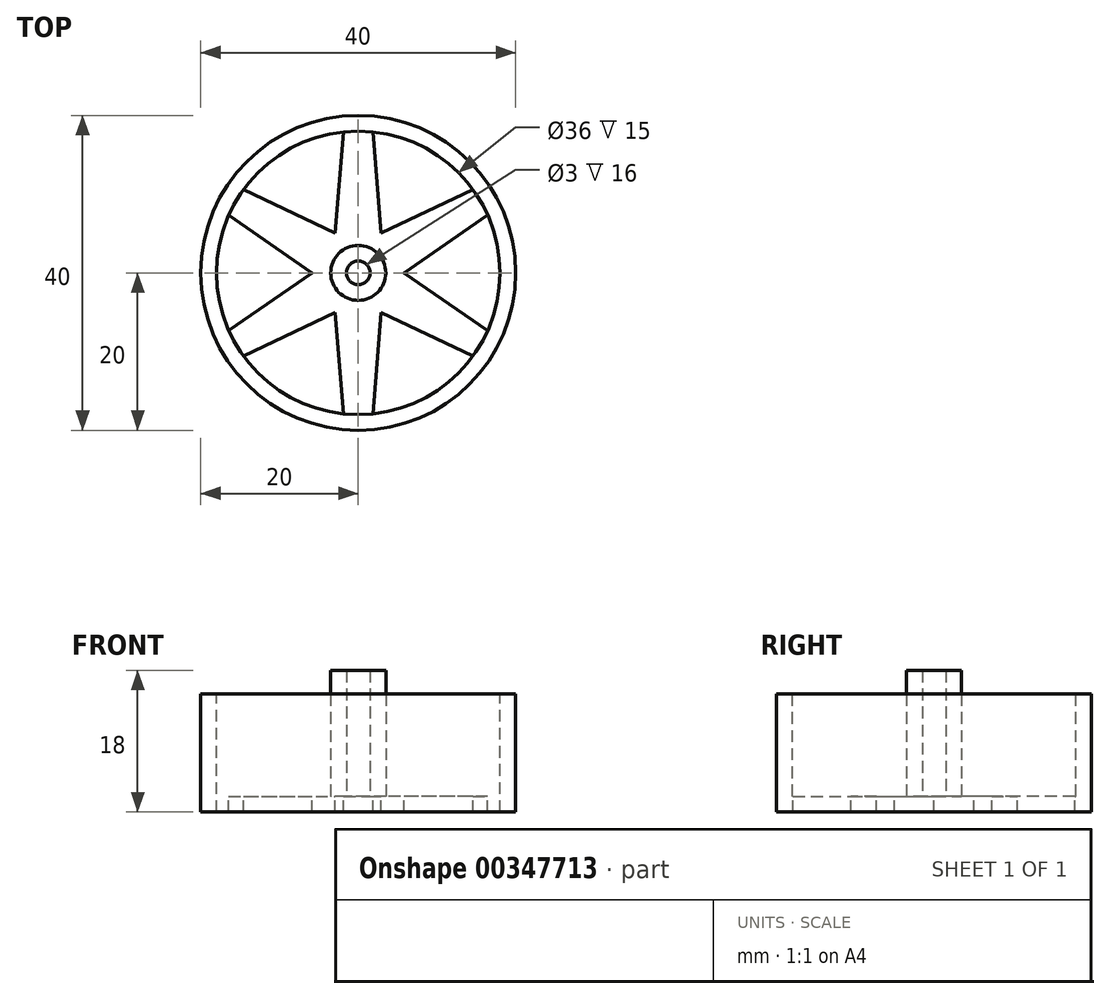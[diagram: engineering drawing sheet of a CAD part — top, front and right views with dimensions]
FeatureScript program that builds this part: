
annotation { "Feature Type Name" : "Feature", "Feature Type Description" : "" }
export const myFeature = defineFeature(function(context is Context, id is Id, definition is map)
    precondition{}
    {
        {
            var Q0;
            Q0=qCreatedBy(makeId("Top.planeOp"),FACE);
            var sketch = newSketch(context, id + "F0", { "sketchPlane" : qUnion([Q0])});
            skCircle(sketch, "E0", {"center": v(0, 0) * mm, "radius": 20 * mm});
            skSolve(sketch);
        }
        {
            var Q0;
            Q0=makeQuery(id+"F0.imprint","IMPRINT",FACE,{"disambiguationData":[TD([[makeQuery(id+"F0.imprint","IMPRINT",EDGE,{"derivedFrom":sQuery(id+"F0.wireOp",EDGE,"E0")}),1.0]])]});
            extrude(context, id + "F1", {"entities" : qUnion([Q0]), "depth" : 15 * mm});
        }
        {
            var Q0;
            Q0=makeQuery(id+"F1.opExtrude","CAP_FACE",FACE,{"disambiguationData":[OSD([sQuery(id+"F0.wireOp",EDGE,"E0")])],"isStart":false});
            var sketch = newSketch(context, id + "F2", { "sketchPlane" : qUnion([Q0])});
            skCircle(sketch, "E1", {"center": v(0, 0) * mm, "radius": 18 * mm});
            skSolve(sketch);
        }
        {
            var Q0;
            Q0=makeQuery(id+"F2.imprint","IMPRINT",FACE,{"disambiguationData":[TD([[makeQuery(id+"F2.imprint","IMPRINT",EDGE,{"derivedFrom":sQuery(id+"F2.wireOp",EDGE,"E1")}),1.0]])]});
            extrude(context, id + "F3", {"entities" : qUnion([Q0]), "operationType" : NewBodyOperationType.REMOVE, "oppositeDirection" : true, "depth" : 13 * mm});
        }
        {
            var Q0;
            Q0=makeQuery(id+"F3.boolean.opBoolean","COPY",FACE,{"derivedFrom":makeQuery(id+"F3.opExtrude","CAP_FACE",FACE,{"disambiguationData":[OSD([sQuery(id+"F2.wireOp",EDGE,"E1")])],"isStart":false})});
            var sketch = newSketch(context, id + "F4", { "sketchPlane" : qUnion([Q0])});
            skCircle(sketch, "E2", {"center": v(0, 0) * mm, "radius": 1.5 * mm});
            skCircle(sketch, "E3", {"center": v(0, 0) * mm, "radius": 3.5 * mm});
            skSolve(sketch);
        }
        {
            var Q0;
            Q0=makeQuery(id+"F4.imprint","IMPRINT",FACE,{"disambiguationData":[TD([[makeQuery(id+"F4.imprint","IMPRINT",EDGE,{"derivedFrom":sQuery(id+"F4.wireOp",EDGE,"E2")}),-1.0]])]});
            extrude(context, id + "F5", {"entities" : qUnion([Q0]), "operationType" : NewBodyOperationType.ADD, "depth" : 16 * mm});
        }
        {
            var Q0;
            {var subQ0=sQuery(id+"F2.wireOp",EDGE,"E1");Q0=makeQuery(id+"F5.boolean.opBoolean","SPLIT",FACE,{"disambiguationData":[TD([makeQuery(id+"F3.boolean.opBoolean","COPY",FACE,{"derivedFrom":makeQuery(id+"F3.opExtrude","SWEPT_FACE",FACE,{"disambiguationData":[OSD([subQ0])]})})])],"derivedFrom":makeQuery(id+"F3.boolean.opBoolean","COPY",FACE,{"derivedFrom":makeQuery(id+"F3.opExtrude","CAP_FACE",FACE,{"disambiguationData":[OSD([subQ0])],"isStart":false})})});}
            var sketch = newSketch(context, id + "F6", { "sketchPlane" : qUnion([Q0])});
            skLineSegment(sketch, "E4", {"start": v(-1.87, 17.9) * mm, "end": v(-3.22, 1.37) * mm});
            skLineSegment(sketch, "E5.MirrorCS", {"start": v(1.87, 17.9) * mm, "end": v(3.22, 1.37) * mm});
            skLineSegment(sketch, "E6.1.0", {"start": v(-16.44, 7.34) * mm, "end": v(-2.8, -2.1) * mm});
            skLineSegment(sketch, "E6.1.1", {"start": v(-14.57, 10.57) * mm, "end": v(0.42, 3.47) * mm});
            skLineSegment(sketch, "E6.2.0", {"start": v(-14.57, -10.57) * mm, "end": v(0.42, -3.47) * mm});
            skLineSegment(sketch, "E6.2.1", {"start": v(-16.44, -7.34) * mm, "end": v(-2.8, 2.1) * mm});
            skLineSegment(sketch, "E6.3.0", {"start": v(1.87, -17.9) * mm, "end": v(3.22, -1.37) * mm});
            skLineSegment(sketch, "E6.3.1", {"start": v(-1.87, -17.9) * mm, "end": v(-3.22, -1.37) * mm});
            skLineSegment(sketch, "E6.4.0", {"start": v(16.44, -7.34) * mm, "end": v(2.8, 2.1) * mm});
            skLineSegment(sketch, "E6.4.1", {"start": v(14.57, -10.57) * mm, "end": v(-0.42, -3.47) * mm});
            skLineSegment(sketch, "E6.5.0", {"start": v(14.57, 10.57) * mm, "end": v(-0.42, 3.47) * mm});
            skLineSegment(sketch, "E6.5.1", {"start": v(16.44, 7.34) * mm, "end": v(2.8, -2.1) * mm});
            skPoint(sketch, "E6.center", {"position": v(0, 0) * mm});
            skSolve(sketch);
        }
        {
            var Q0;
            {var subQ0=sQuery(id+"F6.wireOp",EDGE,"E4");var subQ1=makeQuery(id+"F3.boolean.opBoolean","COPY",EDGE,{"derivedFrom":makeQuery(id+"F3.opExtrude","CAP_EDGE",EDGE,{"disambiguationData":[OSD([sQuery(id+"F2.wireOp",EDGE,"E1")])],"isStart":false})});var subQ2=makeQuery(id+"F6.imprint","INTERSECT",VERTEX,{"derivedFrom":[subQ1,subQ0]});Q0=makeQuery(id+"F6.imprint","IMPRINT",FACE,{"disambiguationData":[TD([[makeQuery(id+"F6.imprint","IMPRINT",EDGE,{"disambiguationData":[TD([[subQ2,-1.0]])],"derivedFrom":subQ0}),-1.0]])]});}
            var Q1;
            {var subQ0=sQuery(id+"F6.wireOp",EDGE,"E5.MirrorCS");var subQ1=makeQuery(id+"F3.boolean.opBoolean","COPY",EDGE,{"derivedFrom":makeQuery(id+"F3.opExtrude","CAP_EDGE",EDGE,{"disambiguationData":[OSD([sQuery(id+"F2.wireOp",EDGE,"E1")])],"isStart":false})});var subQ2=makeQuery(id+"F6.imprint","INTERSECT",VERTEX,{"derivedFrom":[subQ1,subQ0]});Q1=makeQuery(id+"F6.imprint","IMPRINT",FACE,{"disambiguationData":[TD([[makeQuery(id+"F6.imprint","IMPRINT",EDGE,{"disambiguationData":[TD([[subQ2,-1.0]])],"derivedFrom":subQ0}),1.0]])]});}
            var Q2;
            {var subQ0=sQuery(id+"F6.wireOp",EDGE,"E6.4.0");var subQ1=makeQuery(id+"F3.boolean.opBoolean","COPY",EDGE,{"derivedFrom":makeQuery(id+"F3.opExtrude","CAP_EDGE",EDGE,{"disambiguationData":[OSD([sQuery(id+"F2.wireOp",EDGE,"E1")])],"isStart":false})});var subQ2=makeQuery(id+"F6.imprint","INTERSECT",VERTEX,{"derivedFrom":[subQ1,subQ0]});Q2=makeQuery(id+"F6.imprint","IMPRINT",FACE,{"disambiguationData":[TD([[makeQuery(id+"F6.imprint","IMPRINT",EDGE,{"disambiguationData":[TD([[subQ2,-1.0]])],"derivedFrom":subQ0}),-1.0]])]});}
            var Q3;
            {var subQ0=sQuery(id+"F6.wireOp",EDGE,"E6.3.0");var subQ1=makeQuery(id+"F3.boolean.opBoolean","COPY",EDGE,{"derivedFrom":makeQuery(id+"F3.opExtrude","CAP_EDGE",EDGE,{"disambiguationData":[OSD([sQuery(id+"F2.wireOp",EDGE,"E1")])],"isStart":false})});var subQ2=makeQuery(id+"F6.imprint","INTERSECT",VERTEX,{"derivedFrom":[subQ1,subQ0]});Q3=makeQuery(id+"F6.imprint","IMPRINT",FACE,{"disambiguationData":[TD([[makeQuery(id+"F6.imprint","IMPRINT",EDGE,{"disambiguationData":[TD([[subQ2,-1.0]])],"derivedFrom":subQ0}),-1.0]])]});}
            var Q4;
            {var subQ0=sQuery(id+"F6.wireOp",EDGE,"E6.2.0");var subQ1=makeQuery(id+"F3.boolean.opBoolean","COPY",EDGE,{"derivedFrom":makeQuery(id+"F3.opExtrude","CAP_EDGE",EDGE,{"disambiguationData":[OSD([sQuery(id+"F2.wireOp",EDGE,"E1")])],"isStart":false})});var subQ2=makeQuery(id+"F6.imprint","INTERSECT",VERTEX,{"derivedFrom":[subQ1,subQ0]});Q4=makeQuery(id+"F6.imprint","IMPRINT",FACE,{"disambiguationData":[TD([[makeQuery(id+"F6.imprint","IMPRINT",EDGE,{"disambiguationData":[TD([[subQ2,-1.0]])],"derivedFrom":subQ0}),-1.0]])]});}
            var Q5;
            {var subQ0=sQuery(id+"F6.wireOp",EDGE,"E6.1.0");var subQ1=makeQuery(id+"F3.boolean.opBoolean","COPY",EDGE,{"derivedFrom":makeQuery(id+"F3.opExtrude","CAP_EDGE",EDGE,{"disambiguationData":[OSD([sQuery(id+"F2.wireOp",EDGE,"E1")])],"isStart":false})});var subQ2=makeQuery(id+"F6.imprint","INTERSECT",VERTEX,{"derivedFrom":[subQ1,subQ0]});Q5=makeQuery(id+"F6.imprint","IMPRINT",FACE,{"disambiguationData":[TD([[makeQuery(id+"F6.imprint","IMPRINT",EDGE,{"disambiguationData":[TD([[subQ2,-1.0]])],"derivedFrom":subQ0}),-1.0]])]});}
            extrude(context, id + "F7", {"entities" : qUnion([Q0, Q1, Q2, Q3, Q4, Q5]), "operationType" : NewBodyOperationType.REMOVE, "oppositeDirection" : true, "depth" : 2 * mm});
        }
    });
